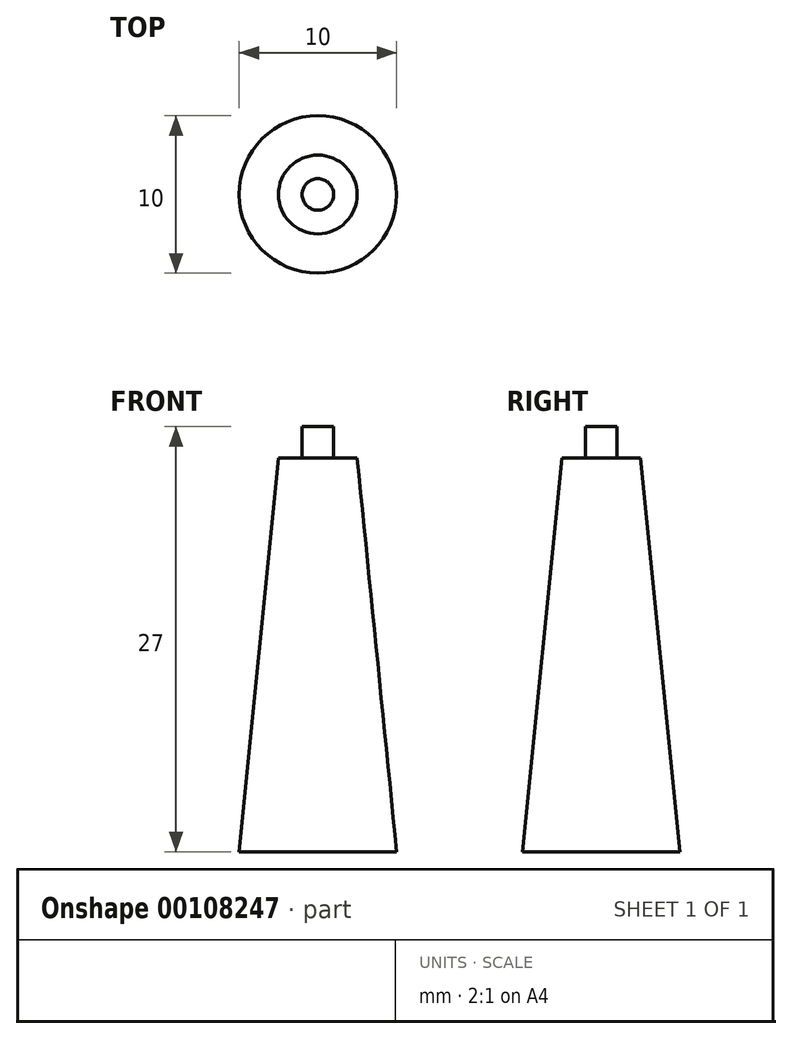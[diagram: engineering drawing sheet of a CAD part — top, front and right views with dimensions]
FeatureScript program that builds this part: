
annotation { "Feature Type Name" : "Feature", "Feature Type Description" : "" }
export const myFeature = defineFeature(function(context is Context, id is Id, definition is map)
    precondition{}
    {
        {
            var Q0;
            Q0=qCreatedBy(makeId("Front.planeOp"),FACE);
            var sketch = newSketch(context, id + "F0", { "sketchPlane" : qUnion([Q0])});
            skLineSegment(sketch, "E0", {"start": v(0, 0) * mm, "end": v(5, 0) * mm});
            skLineSegment(sketch, "E1", {"start": v(5, 0) * mm, "end": v(2.5, 25) * mm});
            skLineSegment(sketch, "E2", {"start": v(2.5, 25) * mm, "end": v(0, 25) * mm});
            skLineSegment(sketch, "E3", {"start": v(0, 25) * mm, "end": v(0, 0) * mm});
            skSolve(sketch);
        }
        {
            var Q0;
            Q0=makeQuery(id+"F0.imprint","IMPRINT",FACE,{"disambiguationData":[TD([[makeQuery(id+"F0.imprint","IMPRINT",EDGE,{"derivedFrom":sQuery(id+"F0.wireOp",EDGE,"E0")}),1.0]])]});
            var Q1;
            Q1=sQuery(id+"F0.wireOp",EDGE,"E3");
            revolve(context, id + "F1", {"entities" : qUnion([Q0]), "axis" : qUnion([Q1]), "revolveType" : RevolveType.FULL});
        }
        {
            var Q0;
            Q0=makeQuery(id+"F1.opRevolve","SWEPT_FACE",FACE,{"disambiguationData":[OSD([sQuery(id+"F0.wireOp",EDGE,"E2")])]});
            var sketch = newSketch(context, id + "F2", { "sketchPlane" : qUnion([Q0])});
            skCircle(sketch, "E4", {"center": v(0, 0) * mm, "radius": 1 * mm});
            skSolve(sketch);
        }
        {
            var Q0;
            Q0=makeQuery(id+"F2.imprint","IMPRINT",FACE,{"disambiguationData":[TD([[makeQuery(id+"F2.imprint","IMPRINT",EDGE,{"derivedFrom":sQuery(id+"F2.wireOp",EDGE,"E4")}),1.0]])]});
            extrude(context, id + "F3", {"entities" : qUnion([Q0]), "operationType" : NewBodyOperationType.ADD, "depth" : 2 * mm});
        }
    });
